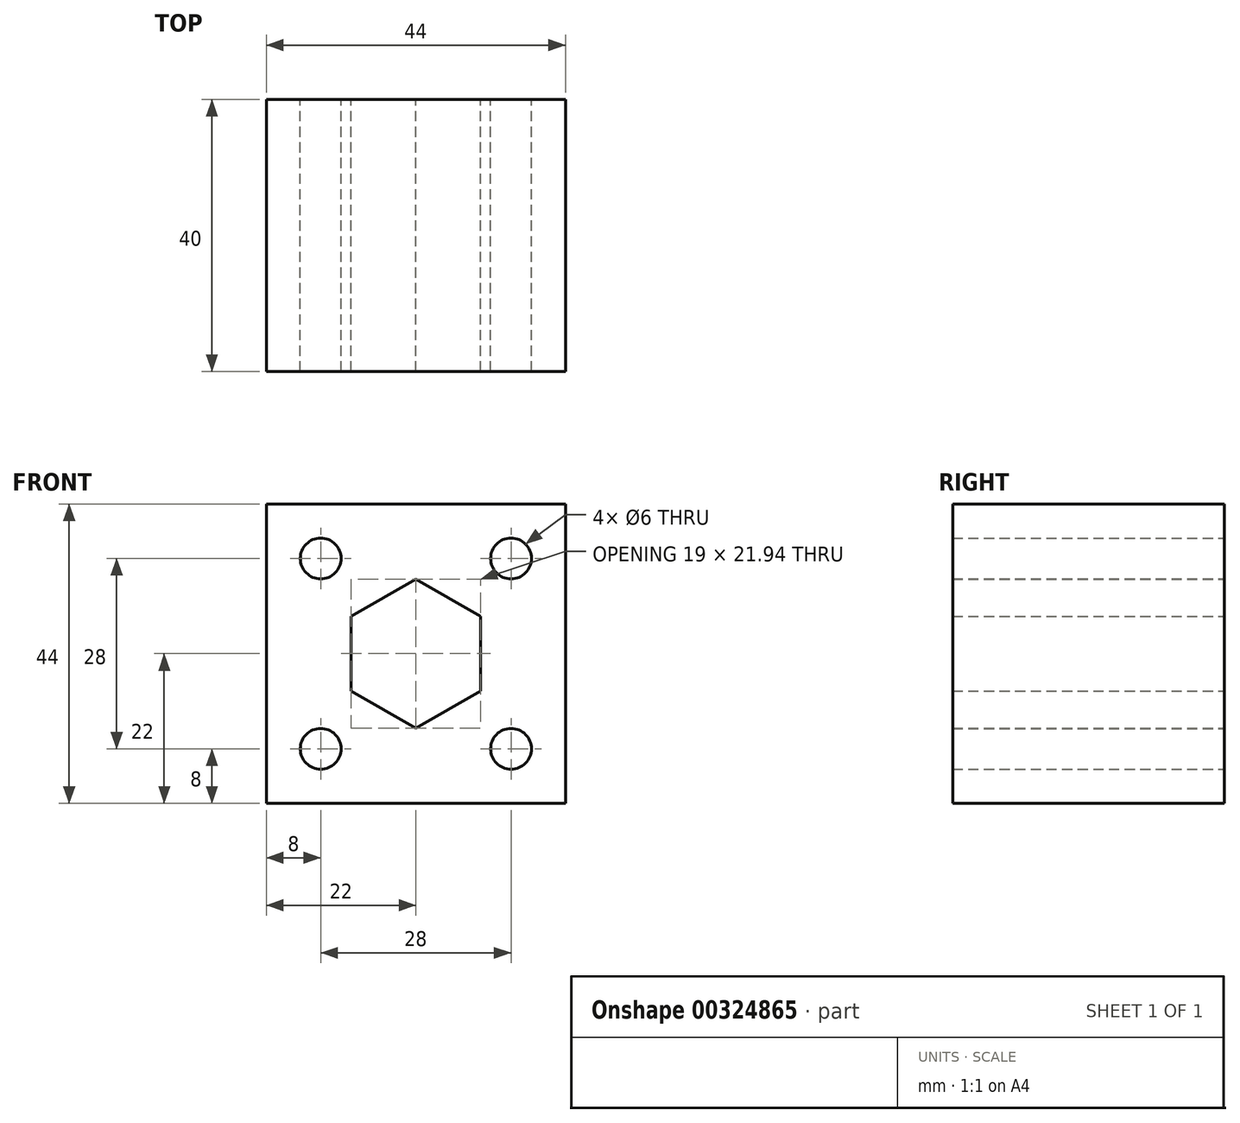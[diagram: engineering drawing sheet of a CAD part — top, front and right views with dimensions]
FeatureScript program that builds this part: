
annotation { "Feature Type Name" : "Feature", "Feature Type Description" : "" }
export const myFeature = defineFeature(function(context is Context, id is Id, definition is map)
    precondition{}
    {
        {
            var Q0;
            Q0=qCreatedBy(makeId("Front.planeOp"),FACE);
            var sketch = newSketch(context, id + "F0", { "sketchPlane" : qUnion([Q0])});
            skLineSegment(sketch, "E0.bottom", {"start": v(-22, 22) * mm, "end": v(22, 22) * mm});
            skLineSegment(sketch, "E0.top", {"start": v(-22, -22) * mm, "end": v(22, -22) * mm});
            skLineSegment(sketch, "E0.left", {"start": v(-22, 22) * mm, "end": v(-22, -22) * mm});
            skLineSegment(sketch, "E0.right", {"start": v(22, 22) * mm, "end": v(22, -22) * mm});
            skPoint(sketch, "E0.middle", {"position": v(0, 0) * mm});
            skLineSegment(sketch, "E1", {"start": v(-22, 22) * mm, "end": v(22, -22) * mm, "construction": true});
            skLineSegment(sketch, "E2", {"start": v(-22, -22) * mm, "end": v(22, 22) * mm, "construction": true});
            skLineSegment(sketch, "E3.bottom", {"start": v(-14, 14) * mm, "end": v(14, 14) * mm, "construction": true});
            skLineSegment(sketch, "E3.top", {"start": v(-14, -14) * mm, "end": v(14, -14) * mm, "construction": true});
            skLineSegment(sketch, "E3.left", {"start": v(-14, 14) * mm, "end": v(-14, -14) * mm, "construction": true});
            skLineSegment(sketch, "E3.right", {"start": v(14, 14) * mm, "end": v(14, -14) * mm, "construction": true});
            skCircle(sketch, "E4", {"center": v(-14, 14) * mm, "radius": 3 * mm});
            skCircle(sketch, "E5", {"center": v(14, 14) * mm, "radius": 3 * mm});
            skCircle(sketch, "E6", {"center": v(-14, -14) * mm, "radius": 3 * mm});
            skCircle(sketch, "E7", {"center": v(14, -14) * mm, "radius": 3 * mm});
            skCircle(sketch, "E8.cCircle", {"center": v(0, 0) * mm, "radius": 9.5 * mm, "construction": true});
            skLineSegment(sketch, "E8.0", {"start": v(9.5, 5.48) * mm, "end": v(9.5, -5.48) * mm});
            skLineSegment(sketch, "E8.1", {"start": v(9.5, -5.48) * mm, "end": v(0, -10.97) * mm});
            skLineSegment(sketch, "E8.2", {"start": v(0, -10.97) * mm, "end": v(-9.5, -5.48) * mm});
            skLineSegment(sketch, "E8.3", {"start": v(-9.5, -5.48) * mm, "end": v(-9.5, 5.48) * mm});
            skLineSegment(sketch, "E8.4", {"start": v(-9.5, 5.48) * mm, "end": v(0, 10.97) * mm});
            skLineSegment(sketch, "E8.5", {"start": v(0, 10.97) * mm, "end": v(9.5, 5.48) * mm});
            skPoint(sketch, "E8.0.midPoint", {"position": v(9.5, 0) * mm});
            skSolve(sketch);
        }
        {
            var Q0;
            Q0=makeQuery(id+"F0.imprint","IMPRINT",FACE,{"disambiguationData":[TD([[makeQuery(id+"F0.imprint","IMPRINT",EDGE,{"derivedFrom":sQuery(id+"F0.wireOp",EDGE,"E0.bottom")}),-1.0]])]});
            extrude(context, id + "F1", {"entities" : qUnion([Q0]), "depth" : 40 * mm, "symmetric" : true});
        }
    });
